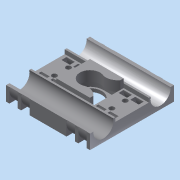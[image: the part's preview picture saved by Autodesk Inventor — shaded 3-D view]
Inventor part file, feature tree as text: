
AUTODESK INVENTOR PART (.ipt)
format: ipt  version: 2015 (Build 190159000, 159)  size: 369,664 bytes
history: native  units: in
note: dims shown in document units (in); Inventor stores cm internally (conversion verified against a paired STEP export)
features: sketch x15, extrude x10, hole x3, projected_geometry x3, pattern_linear x2, revolve x1
ambient origin geometry x8: Origin, YZ Plane, XZ Plane, XY Plane, X Axis, Y Axis, Z Axis, Center Point
bodies: Solid1 (feature_tree)
feature tree (34):
  sketch  "Sketch1"  dims[d0=0.7874in d1=0.7874in]
  extrude  "Extrusion1"  Depth=0.7874in
  hole  "Hole1"  [1 undecoded]
  extrude  "Extrusion2"  Depth=0.3937in
  extrude  "Extrusion3"  Depth=0.0787in
  extrude  "Extrusion4"  Depth=0.3in
  hole  "Hole2"  [1 undecoded]
  extrude  "Extrusion5"  Depth=0.1575in TaperAngle=0.0deg
  hole  "Hole3"  [1 undecoded]
  extrude  "Extrusion6"  Depth=0.5906in
  extrude  "Extrusion7"  Depth=0.4724in
  sketch  "Sketch12"  dims[d39=0.2362in d40=0.2362in]
  extrude  "Extrusion9"  Depth=0.4724in
  extrude  "Extrusion10"  Depth=0.2362in
  extrude  "Extrusion11"  Depth=0.315in TaperAngle=0.0deg
  revolve  "Revolution1"  [1 undecoded]
  pattern_linear  "Rectangular Pattern2"  Spacing1=0.2362in  [1 undecoded]
  pattern_linear  "Rectangular Pattern3"  Spacing1=0.315in  [1 undecoded]
  sketch  "Sketch2"  dims[d2=0.3937in d3=0.2362in d4=0.0in]
  sketch  "Sketch3"  dims[d5=0.4724in d6=0.75in d7=0.375in d8=0.25in d9=0.5635in d10=1.0in d11=0.8108in d12=0.3937in]
  sketch  "Sketch4"  dims[d13=0.0787in d14=0.0787in]
  sketch  "Sketch5"  dims[d16=0.3in d17=0.3in]
  sketch  "Sketch6"  dims[d18=0.2362in d19=0.0in d20=0.6299in]
  sketch  "Sketch7"  dims[d21=0.1575in d22=0.0in d23=0.1575in d24=0.0in]
  sketch  "Sketch8"  dims[d25=0.5512in d26=0.75in d27=0.375in d28=0.25in d29=0.5635in d30=1.0in d31=0.8108in d32=1.9685in]
  sketch  "Sketch9"  dims[d33=1.9685in d34=0.5906in]
  sketch  "Sketch10"  dims[d35=0.5906in d36=0.4724in]
  sketch  "Sketch11"  dims[d37=0.315in d38=0.4724in]
  projected_geometry  "Projected Loop1"
  projected_geometry  "Projected Loop2"
  sketch  "Sketch13"  dims[d41=0.315in d42=1.0in d43=0.0in]
  sketch  "Sketch14"  dims[d44=0.315in d45=0.315in]
  projected_geometry  "Projected Loop3"
  sketch  "Sketch15"  dims[d46=0.2362in d47=0.2362in d48=0.1181in d49=0.75in d50=0.375in d51=0.25in d52=0.5635in d53=1.0in d54=0.8108in d55=0.315in d56=0.315in d57=0.0787in d58=1.0in d59=0.0in d60=0.1969in d61=0.0in d62=0.6693in d63=0.0787in d66=0.0394in d67=0.0in d68=0.0394in d69=0.0in d70=0.0394in d71=0.0in d79=0.2756in d80=0.0787in d81=0.1969in d82=90.0deg d83=0.7874in d85=0.2756in d86=0.7874in d88=1.3386in d89=0.1181in d90=0.0394in d91=0.7874in d93=1.3386in d94=0.2756in]
note: 6 required parameter values undecoded (feature->parameter linkage not recoverable at this tier; creation-order binding heuristic only, values carry confidence <= 0.55)